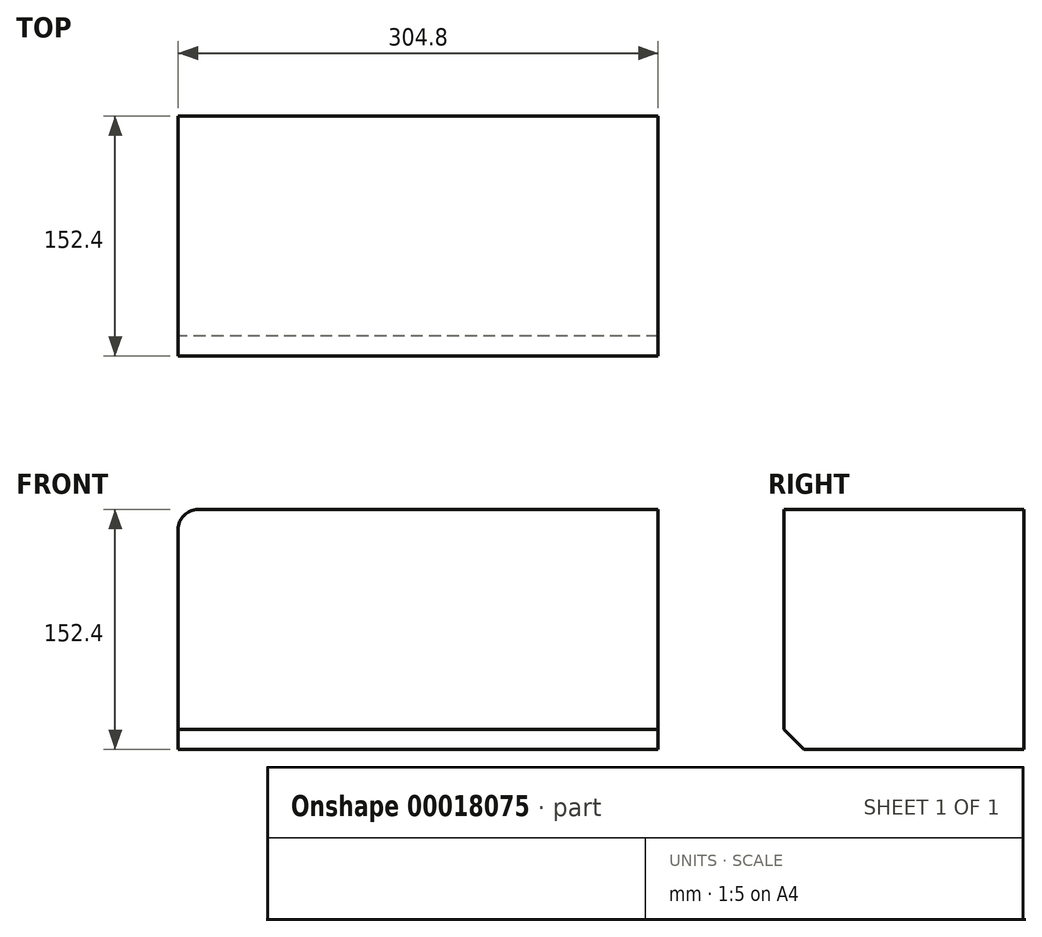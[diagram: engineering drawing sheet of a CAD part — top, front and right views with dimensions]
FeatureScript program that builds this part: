
annotation { "Feature Type Name" : "Feature", "Feature Type Description" : "" }
export const myFeature = defineFeature(function(context is Context, id is Id, definition is map)
    precondition{}
    {
        {
            var Q0;
            Q0=qCreatedBy(makeId("Top.planeOp"),FACE);
            var sketch = newSketch(context, id + "F0", { "sketchPlane" : qUnion([Q0])});
            skLineSegment(sketch, "E0.bottom", {"start": v(-96.33, 114) * mm, "end": v(208.47, 114) * mm});
            skLineSegment(sketch, "E0.top", {"start": v(-96.33, -38.4) * mm, "end": v(208.47, -38.4) * mm});
            skLineSegment(sketch, "E0.left", {"start": v(-96.33, 114) * mm, "end": v(-96.33, -38.4) * mm});
            skLineSegment(sketch, "E0.right", {"start": v(208.47, 114) * mm, "end": v(208.47, -38.4) * mm});
            skSolve(sketch);
        }
        {
            var Q0;
            Q0=makeQuery(id+"F0.imprint","IMPRINT",FACE,{"disambiguationData":[TD([[makeQuery(id+"F0.imprint","IMPRINT",EDGE,{"derivedFrom":sQuery(id+"F0.wireOp",EDGE,"E0.bottom")}),-1.0]])]});
            extrude(context, id + "F1", {"entities" : qUnion([Q0]), "depth" : 152.4 * mm});
        }
        {
            var Q0;
            Q0=makeQuery(id+"F1.opExtrude","CAP_EDGE",EDGE,{"disambiguationData":[OSD([sQuery(id+"F0.wireOp",EDGE,"E0.left")])],"isStart":false});
            fillet(context, id + "F2", {"entities" : qUnion([Q0]), "radius" : 12.7 * mm, "tangentPropagation" : true, "allowEdgeOverflow" : false});
        }
        {
            var Q0;
            Q0=makeQuery(id+"F1.opExtrude","CAP_EDGE",EDGE,{"disambiguationData":[OSD([sQuery(id+"F0.wireOp",EDGE,"E0.top")])],"isStart":true});
            chamfer(context, id + "F3", {"entities" : qUnion([Q0]), "width" : 12.7 * mm, "tangentPropagation" : true});
        }
        {
            var Q0;
            Q0=makeQuery(id+"F1.opExtrude","SWEPT_FACE",FACE,{"disambiguationData":[OSD([sQuery(id+"F0.wireOp",EDGE,"E0.top")])]});
            var sketch = newSketch(context, id + "F4", { "sketchPlane" : qUnion([Q0])});
            skCircle(sketch, "E1", {"center": v(56.07, 101.6) * mm, "radius": 25.4 * mm});
            skSolve(sketch);
        }
    });
